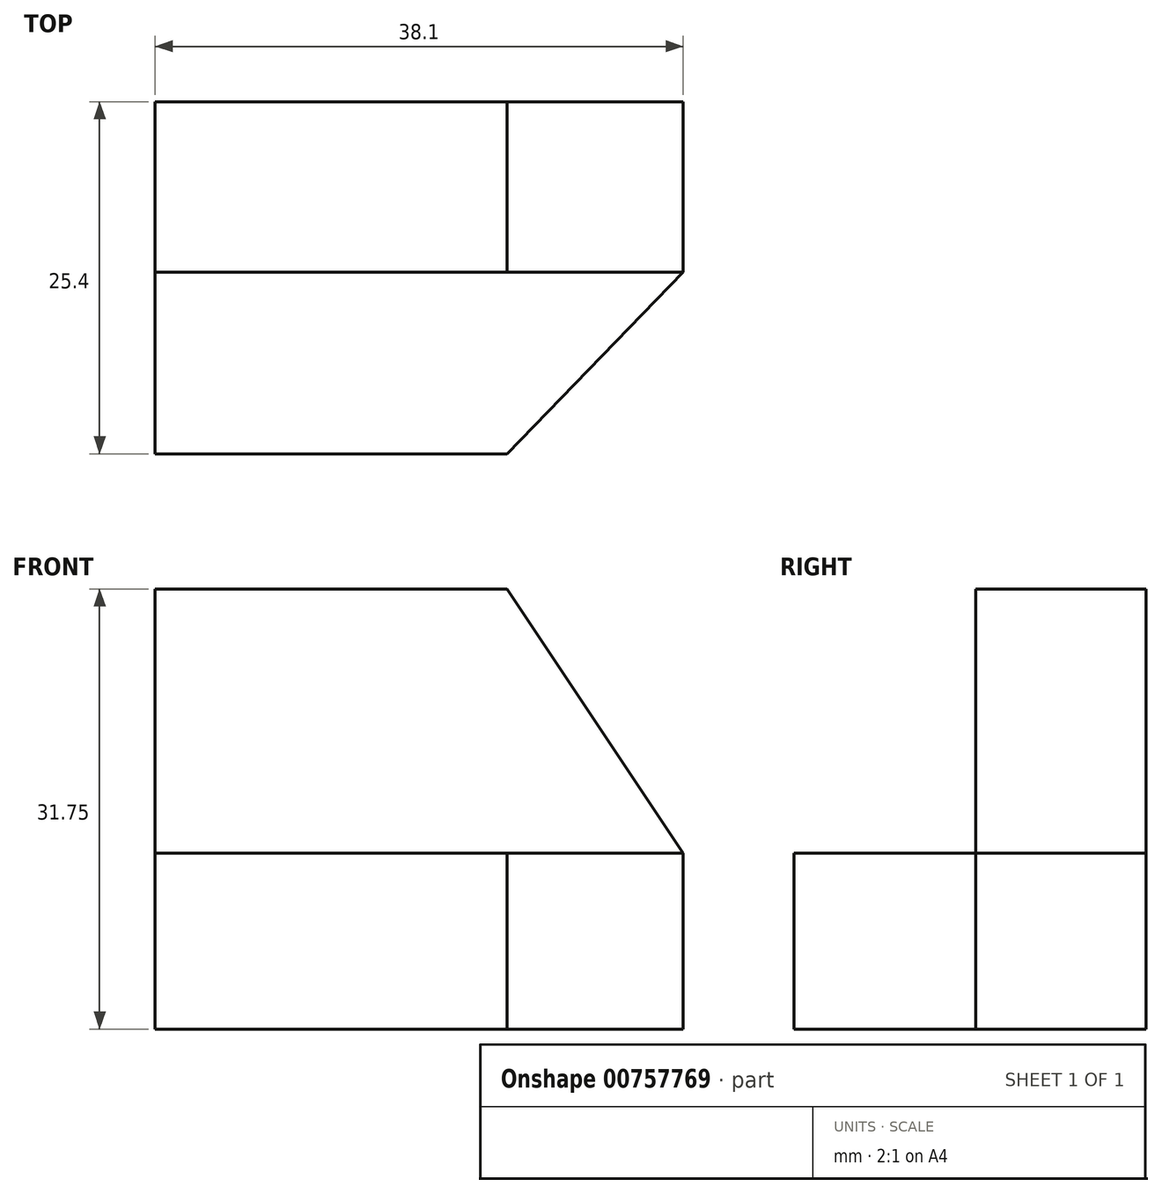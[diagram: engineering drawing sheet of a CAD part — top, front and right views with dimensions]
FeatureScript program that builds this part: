
annotation { "Feature Type Name" : "Feature", "Feature Type Description" : "" }
export const myFeature = defineFeature(function(context is Context, id is Id, definition is map)
    precondition{}
    {
        {
            var Q0;
            Q0=qCreatedBy(makeId("Right.planeOp"),FACE);
            var sketch = newSketch(context, id + "F0", { "sketchPlane" : qUnion([Q0])});
            skLineSegment(sketch, "E0", {"start": v(-13.11, 0) * mm, "end": v(12.29, 0) * mm});
            skLineSegment(sketch, "E1", {"start": v(12.29, 0) * mm, "end": v(12.29, 31.75) * mm});
            skLineSegment(sketch, "E2", {"start": v(12.29, 31.75) * mm, "end": v(-13.11, 31.75) * mm});
            skLineSegment(sketch, "E3", {"start": v(-13.11, 31.75) * mm, "end": v(-13.11, 0) * mm});
            skSolve(sketch);
        }
        {
            var Q0;
            Q0 = qSketchRegion(id + "F0", true);
            extrude(context, id + "F1", {"entities" : qUnion([Q0]), "depth" : 38.1 * mm, "offsetDistance" : 25.4 * mm});
        }
        {
            var Q0;
            Q0=makeQuery(id+"F1.opExtrude","CAP_FACE",FACE,{"disambiguationData":[OSD([sQuery(id+"F0.wireOp",EDGE,"E0"),sQuery(id+"F0.wireOp",EDGE,"E1"),sQuery(id+"F0.wireOp",EDGE,"E2"),sQuery(id+"F0.wireOp",EDGE,"E3")])],"isStart":false});
            var sketch = newSketch(context, id + "F2", { "sketchPlane" : qUnion([Q0])});
            skLineSegment(sketch, "E4", {"start": v(-13.11, 12.7) * mm, "end": v(0, 12.7) * mm});
            skLineSegment(sketch, "E5", {"start": v(0, 12.7) * mm, "end": v(0, 31.75) * mm});
            skSolve(sketch);
        }
        {
            var Q0;
            Q0 = qSketchRegion(id + "F2", true);
            var Q1;
            {var subQ0=sQuery(id+"F2.wireOp",EDGE,"E4");Q1=makeQuery(id+"F2.imprint","IMPRINT",FACE,{"disambiguationData":[TD([[makeQuery(id+"F2.imprint","IMPRINT",EDGE,{"derivedFrom":subQ0}),1.0]])]});}
            extrude(context, id + "F3", {"entities" : qUnion([Q0, Q1]), "operationType" : NewBodyOperationType.REMOVE, "endBound" : BoundingType.THROUGH_ALL, "oppositeDirection" : true, "depth" : 25.4 * mm, "offsetDistance" : 25.4 * mm});
        }
        {
            var Q0;
            Q0=makeQuery(id+"F3.boolean.opBoolean","COPY",FACE,{"derivedFrom":makeQuery(id+"F3.opExtrude","SWEPT_FACE",FACE,{"disambiguationData":[OSD([sQuery(id+"F2.wireOp",EDGE,"E5")])]})});
            var sketch = newSketch(context, id + "F4", { "sketchPlane" : qUnion([Q0])});
            skLineSegment(sketch, "E6", {"start": v(38.1, 12.7) * mm, "end": v(25.4, 31.75) * mm});
            skLineSegment(sketch, "E7", {"start": v(25.4, 31.75) * mm, "end": v(38.1, 31.75) * mm});
            skLineSegment(sketch, "E8", {"start": v(38.1, 31.75) * mm, "end": v(38.1, 12.7) * mm});
            skSolve(sketch);
        }
        {
            var Q0;
            Q0=makeQuery(id+"F4.imprint","IMPRINT",FACE,{"disambiguationData":[TD([[makeQuery(id+"F4.imprint","IMPRINT",EDGE,{"derivedFrom":sQuery(id+"F4.wireOp",EDGE,"E6")}),-1.0]])]});
            extrude(context, id + "F5", {"entities" : qUnion([Q0]), "operationType" : NewBodyOperationType.REMOVE, "endBound" : BoundingType.THROUGH_ALL, "oppositeDirection" : true, "depth" : 25.4 * mm, "offsetDistance" : 25.4 * mm});
        }
        {
            var Q0;
            Q0=makeQuery(id+"F3.boolean.opBoolean","COPY",FACE,{"derivedFrom":makeQuery(id+"F3.opExtrude","SWEPT_FACE",FACE,{"disambiguationData":[OSD([sQuery(id+"F2.wireOp",EDGE,"E4")])]})});
            var sketch = newSketch(context, id + "F6", { "sketchPlane" : qUnion([Q0])});
            skLineSegment(sketch, "E9", {"start": v(38.1, 0) * mm, "end": v(25.4, -13.11) * mm});
            skLineSegment(sketch, "E10", {"start": v(25.4, -13.11) * mm, "end": v(38.1, -13.11) * mm});
            skLineSegment(sketch, "E11", {"start": v(38.1, -13.11) * mm, "end": v(38.1, 0) * mm});
            skSolve(sketch);
        }
        {
            var Q0;
            Q0 = qSketchRegion(id + "F6", true);
            extrude(context, id + "F7", {"entities" : qUnion([Q0]), "operationType" : NewBodyOperationType.REMOVE, "oppositeDirection" : true, "depth" : 25.4 * mm, "offsetDistance" : 25.4 * mm});
        }
    });
